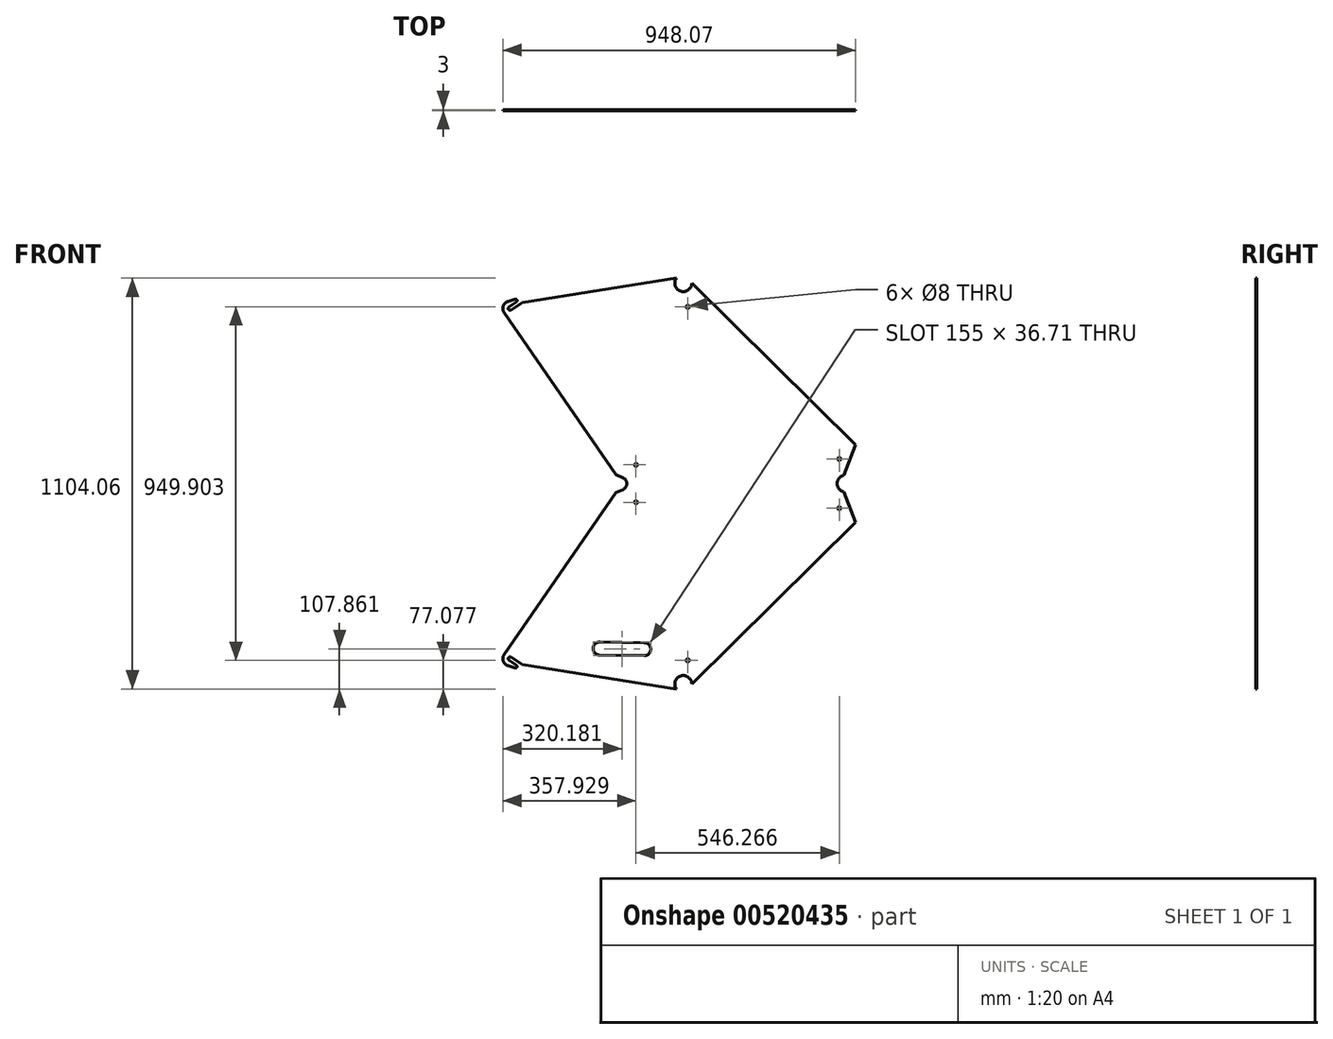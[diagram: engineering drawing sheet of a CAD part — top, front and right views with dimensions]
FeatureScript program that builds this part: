
annotation { "Feature Type Name" : "Feature", "Feature Type Description" : "" }
export const myFeature = defineFeature(function(context is Context, id is Id, definition is map)
    precondition{}
    {
        {
            var Q0;
            Q0=qCreatedBy(makeId("Front.planeOp"),FACE);
            var sketch = newSketch(context, id + "F0", { "sketchPlane" : qUnion([Q0])});
            skCircle(sketch, "E0", {"center": v(1053.9, -134.2) * mm, "radius": 17 * mm, "construction": true});
            skCircle(sketch, "E1", {"center": v(1053.9, -134.2) * mm, "radius": 21.5 * mm, "construction": true});
            skLineSegment(sketch, "E2", {"start": v(622.48, -20.32) * mm, "end": v(871.92, 345.36) * mm, "construction": true});
            skLineSegment(sketch, "E3", {"start": v(615.02, -14.4) * mm, "end": v(879.24, 372.95) * mm, "construction": true});
            skLineSegment(sketch, "E4", {"start": v(1053.9, -134.2) * mm, "end": v(865.03, 414.2) * mm, "construction": true});
            skLineSegment(sketch, "E5", {"start": v(1034.15, -125.7) * mm, "end": v(850, 409.01) * mm, "construction": true});
            skLineSegment(sketch, "E6", {"start": v(861.66, 381.3) * mm, "end": v(851.9, 409.67) * mm, "construction": true});
            skLineSegment(sketch, "E7", {"start": v(1064.21, -115.34) * mm, "end": v(880.07, 419.37) * mm, "construction": true});
            skLineSegment(sketch, "E8", {"start": v(1053.9, -134.2) * mm, "end": v(645.8, -73.78) * mm, "construction": true});
            skLineSegment(sketch, "E9", {"start": v(743.09, -99.4) * mm, "end": v(644.17, -84.76) * mm, "construction": true});
            skLineSegment(sketch, "E10", {"start": v(746.34, -77.44) * mm, "end": v(647.42, -62.8) * mm, "construction": true});
            skLineSegment(sketch, "E11", {"start": v(1035.36, -145.1) * mm, "end": v(841.66, -116.43) * mm, "construction": true});
            skLineSegment(sketch, "E12", {"start": v(1039.32, -118.4) * mm, "end": v(845.61, -89.72) * mm, "construction": true});
            skLineSegment(sketch, "E13", {"start": v(966.15, -134.86) * mm, "end": v(995.58, -139.21) * mm, "construction": true});
            skLineSegment(sketch, "E14", {"start": v(960.23, -139.03) * mm, "end": v(994.85, -144.16) * mm, "construction": true});
            skLineSegment(sketch, "E15", {"start": v(963.6, -143.58) * mm, "end": v(964.04, -140.6) * mm, "construction": true});
            skArc(sketch, "E16", {"start": v(959.64, -143) * mm, "mid": v(959.83, -143.73) * mm, "end": v(960.48, -144.13) * mm, "construction": true});
            skLineSegment(sketch, "E17", {"start": v(960.48, -144.13) * mm, "end": v(962.46, -144.42) * mm, "construction": true});
            skArc(sketch, "E18", {"start": v(962.46, -144.42) * mm, "mid": v(963.2, -144.23) * mm, "end": v(963.6, -143.58) * mm, "construction": true});
            skLineSegment(sketch, "E19", {"start": v(965.3, -133.72) * mm, "end": v(967.21, -120.86) * mm, "construction": true});
            skLineSegment(sketch, "E20", {"start": v(963, -120.24) * mm, "end": v(959.64, -143) * mm, "construction": true});
            skLineSegment(sketch, "E21", {"start": v(962.42, -124.2) * mm, "end": v(966.63, -124.82) * mm, "construction": true});
            skArc(sketch, "E22", {"start": v(965.17, -139.77) * mm, "mid": v(964.43, -139.95) * mm, "end": v(964.04, -140.6) * mm, "construction": true});
            skLineSegment(sketch, "E23", {"start": v(961.7, -129.14) * mm, "end": v(965.9, -129.76) * mm, "construction": true});
            skLineSegment(sketch, "E24", {"start": v(960.08, -126.38) * mm, "end": v(968.24, -127.58) * mm, "construction": true});
            skLineSegment(sketch, "E25", {"start": v(974.82, -141.2) * mm, "end": v(975.55, -136.25) * mm, "construction": true});
            skArc(sketch, "E26", {"start": v(965.3, -133.72) * mm, "mid": v(965.5, -134.46) * mm, "end": v(966.15, -134.86) * mm, "construction": true});
            skLineSegment(sketch, "E27", {"start": v(964.14, -119.4) * mm, "end": v(966.37, -119.73) * mm, "construction": true});
            skArc(sketch, "E28", {"start": v(964.14, -119.4) * mm, "mid": v(963.4, -119.58) * mm, "end": v(963, -120.24) * mm, "construction": true});
            skArc(sketch, "E29", {"start": v(967.21, -120.86) * mm, "mid": v(967.03, -120.12) * mm, "end": v(966.37, -119.73) * mm, "construction": true});
            skLineSegment(sketch, "E30", {"start": v(995.58, -139.21) * mm, "end": v(999.8, -144.9) * mm, "construction": true});
            skLineSegment(sketch, "E31", {"start": v(979.72, -143.94) * mm, "end": v(981.04, -135.04) * mm, "construction": true});
            skArc(sketch, "E32", {"start": v(995.7, -145.3) * mm, "mid": v(995.5, -144.55) * mm, "end": v(994.85, -144.16) * mm, "construction": true});
            skArc(sketch, "E33", {"start": v(995.25, -148.26) * mm, "mid": v(995.44, -149) * mm, "end": v(996.1, -149.4) * mm, "construction": true});
            skArc(sketch, "E34", {"start": v(998.07, -149.7) * mm, "mid": v(998.82, -149.5) * mm, "end": v(999.2, -148.85) * mm, "construction": true});
            skLineSegment(sketch, "E35", {"start": v(996.1, -149.4) * mm, "end": v(998.07, -149.7) * mm, "construction": true});
            skLineSegment(sketch, "E36", {"start": v(999.2, -148.85) * mm, "end": v(999.8, -144.9) * mm, "construction": true});
            skLineSegment(sketch, "E37", {"start": v(995.25, -148.26) * mm, "end": v(995.7, -145.3) * mm, "construction": true});
            skLineSegment(sketch, "E38", {"start": v(985.2, -142.73) * mm, "end": v(985.94, -137.79) * mm, "construction": true});
            skLineSegment(sketch, "E39", {"start": v(995.47, -146.78) * mm, "end": v(993.6, -159.38) * mm, "construction": true});
            skLineSegment(sketch, "E40", {"start": v(850, 409.01) * mm, "end": v(880.07, 419.37) * mm, "construction": true});
            skLineSegment(sketch, "E41", {"start": v(859.77, 380.65) * mm, "end": v(861.66, 381.3) * mm, "construction": true});
            skLineSegment(sketch, "E42", {"start": v(1053.92, -134.2) * mm, "end": v(1520.05, 326.73) * mm, "construction": true});
            skLineSegment(sketch, "E43", {"start": v(1076.92, -133.82) * mm, "end": v(1510.36, 294.78) * mm, "construction": true});
            skLineSegment(sketch, "E44", {"start": v(1060.7, -105.14) * mm, "end": v(1497.91, 327.2) * mm, "construction": true});
            skLineSegment(sketch, "E45", {"start": v(879.24, 372.95) * mm, "end": v(1402.67, 372.95) * mm, "construction": true});
            skLineSegment(sketch, "E46", {"start": v(901.53, 357.05) * mm, "end": v(1486.45, 357.05) * mm, "construction": true});
            skLineSegment(sketch, "E47", {"start": v(890.58, 388.85) * mm, "end": v(1474.25, 388.85) * mm, "construction": true});
            skArc(sketch, "E48", {"start": v(1486.5, 356.93) * mm, "mid": v(1487.54, 375.64) * mm, "end": v(1474.25, 388.85) * mm, "construction": true});
            skArc(sketch, "E49", {"start": v(890.58, 388.85) * mm, "mid": v(888.92, 370.5) * mm, "end": v(901.53, 357.05) * mm, "construction": true});
            skArc(sketch, "E50", {"start": v(1510.36, 294.78) * mm, "mid": v(1511.76, 313.92) * mm, "end": v(1497.91, 327.2) * mm, "construction": true});
            skArc(sketch, "E51", {"start": v(919.09, -223.5) * mm, "mid": v(918.34, -223.31) * mm, "end": v(917.6, -223.13) * mm, "construction": true});
            skFitSpline(sketch, "E52", {"points": [v(871.92, 345.36) * mm, v(875.7, 355.52) * mm, v(881.2, 370.3) * mm, v(868.26, 368.37) * mm, v(864.2, 367.77) * mm], "construction": true});
            skArc(sketch, "E53", {"start": v(591.11, -61.72) * mm, "mid": v(584.1, -63.16) * mm, "end": v(585.54, -70.17) * mm});
            skLineSegment(sketch, "E54", {"start": v(585.54, -70.17) * mm, "end": v(605.08, -83.05) * mm});
            skLineSegment(sketch, "E55", {"start": v(601.2, -91.02) * mm, "end": v(582.02, -84.5) * mm});
            skLineSegment(sketch, "E56", {"start": v(584.15, -63.19) * mm, "end": v(613.37, -82.46) * mm, "construction": true});
            skLineSegment(sketch, "E57", {"start": v(607.46, -8.63) * mm, "end": v(607.4, -8.7) * mm, "construction": true});
            skLineSegment(sketch, "E58", {"start": v(644.18, -84.66) * mm, "end": v(644.29, -83.94) * mm, "construction": true});
            skLineSegment(sketch, "E59", {"start": v(591.11, -61.72) * mm, "end": v(620.67, -81.2) * mm});
            skLineSegment(sketch, "E60", {"start": v(644.18, -84.66) * mm, "end": v(622.66, -81.47) * mm, "construction": true});
            skArc(sketch, "E61", {"start": v(644.63, -83.68) * mm, "mid": v(644.4, -83.74) * mm, "end": v(644.29, -83.94) * mm, "construction": true});
            skLineSegment(sketch, "E62", {"start": v(644.18, -84.66) * mm, "end": v(644.19, -84.63) * mm, "construction": true});
            skArc(sketch, "E63", {"start": v(601.2, -91.02) * mm, "mid": v(606.49, -88.67) * mm, "end": v(605.08, -83.05) * mm});
            skArc(sketch, "E64", {"start": v(617.78, -52.64) * mm, "mid": v(628.06, -58.54) * mm, "end": v(639.47, -61.73) * mm, "construction": true});
            skLineSegment(sketch, "E65", {"start": v(670.48, -77.43) * mm, "end": v(577.33, -63.64) * mm, "construction": true});
            skLineSegment(sketch, "E66", {"start": v(647.4, -62.9) * mm, "end": v(639.47, -61.73) * mm, "construction": true});
            skArc(sketch, "E67", {"start": v(647.3, -63.56) * mm, "mid": v(647.36, -63.78) * mm, "end": v(647.56, -63.9) * mm, "construction": true});
            skLineSegment(sketch, "E68", {"start": v(647.3, -63.56) * mm, "end": v(647.4, -62.9) * mm, "construction": true});
            skArc(sketch, "E69", {"start": v(614, -32.51) * mm, "mid": v(611.92, -43.32) * mm, "end": v(617.78, -52.64) * mm, "construction": true});
            skLineSegment(sketch, "E70", {"start": v(614, -32.51) * mm, "end": v(622.56, -20.17) * mm, "construction": true});
            skLineSegment(sketch, "E71", {"start": v(577.33, -63.64) * mm, "end": v(629.71, 4.8) * mm, "construction": true});
            skArc(sketch, "E72", {"start": v(572.75, -54.03) * mm, "mid": v(569.56, -71.65) * mm, "end": v(582.02, -84.5) * mm});
            skLineSegment(sketch, "E73", {"start": v(607.46, -8.63) * mm, "end": v(608.42, -9.36) * mm, "construction": true});
            skArc(sketch, "E74", {"start": v(621.55, -19.02) * mm, "mid": v(621.5, -19.24) * mm, "end": v(621.6, -19.44) * mm, "construction": true});
            skLineSegment(sketch, "E75", {"start": v(621.6, -19.44) * mm, "end": v(622.56, -20.17) * mm, "construction": true});
            skArc(sketch, "E76", {"start": v(608.42, -9.36) * mm, "mid": v(608.64, -9.42) * mm, "end": v(608.84, -9.3) * mm, "construction": true});
            skLineSegment(sketch, "E77", {"start": v(608.42, -9.36) * mm, "end": v(607.46, -8.63) * mm, "construction": true});
            skLineSegment(sketch, "E78", {"start": v(619.71, -24.29) * mm, "end": v(604.42, -12.6) * mm, "construction": true});
            skCircle(sketch, "E79", {"center": v(600.85, -74.2) * mm, "radius": 5 * mm, "construction": true});
            skLineSegment(sketch, "E80", {"start": v(621.6, -19.44) * mm, "end": v(608.42, -9.36) * mm, "construction": true});
            skLineSegment(sketch, "E81", {"start": v(841.66, -116.43) * mm, "end": v(743.09, -99.4) * mm, "construction": true});
            skLineSegment(sketch, "E82", {"start": v(746.34, -77.44) * mm, "end": v(845.61, -89.72) * mm, "construction": true});
            skEllipse(sketch, "E83", {"center": v(843.64, -103.07) * mm, "majorRadius": 13.5 * mm, "minorRadius": 8.5 * mm, "majorAxis": v(-0.15, -0.99), "construction": true});
            skCircle(sketch, "E84", {"center": v(795.03, 249.5) * mm, "radius": 9.5 * mm, "construction": true});
            skLineSegment(sketch, "E85", {"start": v(796.02, 244.3) * mm, "end": v(795.95, 244.64) * mm, "construction": true});
            skLineSegment(sketch, "E86", {"start": v(796.02, 244.3) * mm, "end": v(789.82, 248.52) * mm, "construction": true});
            skLineSegment(sketch, "E87", {"start": v(784, 242.2) * mm, "end": v(792.26, 236.56) * mm, "construction": true});
            skLineSegment(sketch, "E88", {"start": v(792.26, 236.56) * mm, "end": v(793.8, 238.84) * mm, "construction": true});
            skLineSegment(sketch, "E89", {"start": v(791.91, 236.5) * mm, "end": v(792.26, 236.56) * mm, "construction": true});
            skLineSegment(sketch, "E90", {"start": v(795.95, 244.64) * mm, "end": v(790.17, 248.58) * mm, "construction": true});
            skLineSegment(sketch, "E91", {"start": v(791.91, 236.5) * mm, "end": v(784.06, 241.85) * mm, "construction": true});
            skLineSegment(sketch, "E92", {"start": v(789.96, 238.43) * mm, "end": v(794.75, 245.46) * mm, "construction": true});
            skLineSegment(sketch, "E93", {"start": v(790.2, 238) * mm, "end": v(795.12, 245.2) * mm, "construction": true});
            skLineSegment(sketch, "E94", {"start": v(793.8, 238.84) * mm, "end": v(785.55, 244.47) * mm, "construction": true});
            skLineSegment(sketch, "E95", {"start": v(792.78, 239.54) * mm, "end": v(796.02, 244.3) * mm, "construction": true});
            skArc(sketch, "E96", {"start": v(962.06, -126.67) * mm, "mid": v(930.44, 82.62) * mm, "end": v(787.99, 239.18) * mm, "construction": true});
            skLineSegment(sketch, "E97", {"start": v(702.12, -93.34) * mm, "end": v(670.46, -88.65) * mm, "construction": true});
            skCircle(sketch, "E98", {"center": v(1054.53, -129.2) * mm, "radius": 89.9 * mm, "construction": true});
            skCircle(sketch, "E99", {"center": v(600.85, -74.2) * mm, "radius": 41.4 * mm, "construction": true});
            skLineSegment(sketch, "E100", {"start": v(1055.81, -39.3) * mm, "end": v(601.44, -32.8) * mm, "construction": true});
            skLineSegment(sketch, "E101", {"start": v(1469.36, 401.56) * mm, "end": v(1507.64, 416.26) * mm, "construction": true});
            skLineSegment(sketch, "E102", {"start": v(1507.64, 416.26) * mm, "end": v(1552.44, 299.56) * mm, "construction": true});
            skLineSegment(sketch, "E103", {"start": v(1552.44, 299.56) * mm, "end": v(1514.16, 284.87) * mm, "construction": true});
            skLineSegment(sketch, "E104", {"start": v(1514.16, 284.87) * mm, "end": v(1469.36, 401.56) * mm, "construction": true});
            skLineSegment(sketch, "E105", {"start": v(1516.78, 301.13) * mm, "end": v(1076.92, -133.82) * mm});
            skLineSegment(sketch, "E106", {"start": v(572.75, -54.03) * mm, "end": v(878.77, 388.85) * mm});
            skArc(sketch, "E107", {"start": v(1076.92, -133.82) * mm, "mid": v(1046.89, -112.3) * mm, "end": v(1035, -147.28) * mm});
            skLineSegment(sketch, "E108.trimOffspring", {"start": v(1035, -147.28) * mm, "end": v(620.67, -81.2) * mm});
            skCircle(sketch, "E109", {"center": v(926.64, 354.5) * mm, "radius": 4 * mm});
            skCircle(sketch, "E110", {"center": v(1472.9, 338.57) * mm, "radius": 4 * mm});
            skCircle(sketch, "E111", {"center": v(1065.92, -70.2) * mm, "radius": 4 * mm});
            skLineSegment(sketch, "E112", {"start": v(1053.92, -134.2) * mm, "end": v(1237.3, -134.2) * mm, "construction": true});
            skLineSegment(sketch, "E113", {"start": v(1053.92, -134.2) * mm, "end": v(1053.92, 23.57) * mm, "construction": true});
            skCircle(sketch, "E114", {"center": v(866.64, 414.5) * mm, "radius": 25 * mm, "construction": true});
            skCircle(sketch, "E115", {"center": v(1489.1, 401.54) * mm, "radius": 28.6 * mm, "construction": true});
            skLineSegment(sketch, "E116", {"start": v(1516.78, 301.13) * mm, "end": v(1482.36, 388.85) * mm});
            skLineSegment(sketch, "E117.trimOffspring", {"start": v(878.77, 388.85) * mm, "end": v(1482.36, 388.85) * mm});
            skSolve(sketch);
        }
        {
            var Q0;
            Q0 = qSketchRegion(id + "F0", true);
            extrude(context, id + "F1", {"entities" : qUnion([Q0]), "depth" : 3 * mm, "offsetDistance" : 25 * mm});
        }
        {
            var Q0;
            Q0=makeQuery(id+"F1.opExtrude","SWEPT_FACE",FACE,{"disambiguationData":[OSD([sQuery(id+"F0.wireOp",EDGE,"E117.trimOffspring")])]});
            cPlane(context, id + "F2", {"entities" : qUnion([Q0]), "cplaneType" : CPlaneType.OFFSET, "offset" : 15.9 * mm, "width" : 150 * mm, "height" : 150 * mm});
        }
        {
            var Q0;
            Q0=makeQuery(id+"F1.opExtrude","SWEPT_BODY",BODY,{"disambiguationData":[OSD([sQuery(id+"F0.wireOp",EDGE,"E53"),sQuery(id+"F0.wireOp",EDGE,"E54"),sQuery(id+"F0.wireOp",EDGE,"E55"),sQuery(id+"F0.wireOp",EDGE,"E59"),sQuery(id+"F0.wireOp",EDGE,"c0fece56-cd10-4327-9040-2cab23e675d4"),sQuery(id+"F0.wireOp",EDGE,"E63"),sQuery(id+"F0.wireOp",EDGE,"E72"),sQuery(id+"F0.wireOp",EDGE,"PVY0APLz-6rdr-JrDk-CvCb-vWmYWycaJObT"),sQuery(id+"F0.wireOp",EDGE,"rSiPkJzu-22ck-wLmw-T34Z-YrS7vC3DeLN9"),sQuery(id+"F0.wireOp",EDGE,"E105"),sQuery(id+"F0.wireOp",EDGE,"E106"),sQuery(id+"F0.wireOp",EDGE,"E107"),sQuery(id+"F0.wireOp",EDGE,"E108.trimOffspring")])]});
            var Q1;
            Q1=qCreatedBy(id+"F2.planeOp",FACE);
            mirror(context, id + "F3", {"entities" : qUnion([Q0]), "mirrorPlane" : qUnion([Q1])});
        }
        {
            var Q0;
            Q0=makeQuery(id+"F1.opExtrude","CAP_FACE",FACE,{"disambiguationData":[OSD([sQuery(id+"F0.wireOp",EDGE,"E53"),sQuery(id+"F0.wireOp",EDGE,"E54"),sQuery(id+"F0.wireOp",EDGE,"E55"),sQuery(id+"F0.wireOp",EDGE,"E59"),sQuery(id+"F0.wireOp",EDGE,"c0fece56-cd10-4327-9040-2cab23e675d4"),sQuery(id+"F0.wireOp",EDGE,"E63"),sQuery(id+"F0.wireOp",EDGE,"E72"),sQuery(id+"F0.wireOp",EDGE,"PVY0APLz-6rdr-JrDk-CvCb-vWmYWycaJObT"),sQuery(id+"F0.wireOp",EDGE,"rSiPkJzu-22ck-wLmw-T34Z-YrS7vC3DeLN9"),sQuery(id+"F0.wireOp",EDGE,"E105"),sQuery(id+"F0.wireOp",EDGE,"E106"),sQuery(id+"F0.wireOp",EDGE,"E107"),sQuery(id+"F0.wireOp",EDGE,"E108.trimOffspring")])],"isStart":false});
            var sketch = newSketch(context, id + "F4", { "sketchPlane" : qUnion([Q0])});
            skArc(sketch, "E118", {"start": v(1484.73, 426.68) * mm, "mid": v(1467.24, 404.75) * mm, "end": v(1484.73, 382.81) * mm});
            skArc(sketch, "E119", {"start": v(891.59, 388.85) * mm, "mid": v(901.78, 404.75) * mm, "end": v(891.59, 420.65) * mm});
            skLineSegment(sketch, "E120", {"start": v(884.28, 404.75) * mm, "end": v(1489.74, 404.75) * mm, "construction": true});
            skLineSegment(sketch, "E121", {"start": v(891.59, 420.65) * mm, "end": v(872.8, 429.29) * mm});
            skLineSegment(sketch, "E122", {"start": v(891.59, 388.85) * mm, "end": v(872.8, 380.21) * mm});
            skLineSegment(sketch, "E123.0", {"start": v(1516.78, 508.37) * mm, "end": v(1482.36, 420.65) * mm, "construction": true});
            skLineSegment(sketch, "E124", {"start": v(1482.36, 388.85) * mm, "end": v(1516.78, 301.13) * mm, "construction": true});
            skLineSegment(sketch, "E125", {"start": v(891.59, 420.65) * mm, "end": v(1473.82, 420.65) * mm});
            skLineSegment(sketch, "E126", {"start": v(891.59, 388.85) * mm, "end": v(1473.82, 388.85) * mm});
            skSolve(sketch);
        }
        {
            var Q0;
            Q0 = qSketchRegion(id + "F4", true);
            var Q1;
            Q1=makeQuery(id+"F3.opPattern","COPY",FACE,{"derivedFrom":makeQuery(id+"F1.opExtrude","CAP_FACE",FACE,{"disambiguationData":[OSD([sQuery(id+"F0.wireOp",EDGE,"E53"),sQuery(id+"F0.wireOp",EDGE,"E54"),sQuery(id+"F0.wireOp",EDGE,"E55"),sQuery(id+"F0.wireOp",EDGE,"E59"),sQuery(id+"F0.wireOp",EDGE,"c0fece56-cd10-4327-9040-2cab23e675d4"),sQuery(id+"F0.wireOp",EDGE,"E63"),sQuery(id+"F0.wireOp",EDGE,"E72"),sQuery(id+"F0.wireOp",EDGE,"PVY0APLz-6rdr-JrDk-CvCb-vWmYWycaJObT"),sQuery(id+"F0.wireOp",EDGE,"rSiPkJzu-22ck-wLmw-T34Z-YrS7vC3DeLN9"),sQuery(id+"F0.wireOp",EDGE,"E105"),sQuery(id+"F0.wireOp",EDGE,"E106"),sQuery(id+"F0.wireOp",EDGE,"E107"),sQuery(id+"F0.wireOp",EDGE,"E108.trimOffspring")])],"isStart":true}),"instanceName":"1"});
            extrude(context, id + "F5", {"entities" : qUnion([Q0]), "operationType" : NewBodyOperationType.ADD, "endBound" : BoundingType.UP_TO_SURFACE, "oppositeDirection" : true, "depth" : 65 * mm, "endBoundEntityFace" : qUnion([Q1]), "offsetDistance" : 25 * mm});
        }
        {
            var Q0;
            {var subQ0=makeQuery(id+"F1.opExtrude","CAP_FACE",FACE,{"disambiguationData":[OSD([sQuery(id+"F0.wireOp",EDGE,"E53"),sQuery(id+"F0.wireOp",EDGE,"E54"),sQuery(id+"F0.wireOp",EDGE,"E55"),sQuery(id+"F0.wireOp",EDGE,"E59"),sQuery(id+"F0.wireOp",EDGE,"E63"),sQuery(id+"F0.wireOp",EDGE,"E72"),sQuery(id+"F0.wireOp",EDGE,"E105"),sQuery(id+"F0.wireOp",EDGE,"E106"),sQuery(id+"F0.wireOp",EDGE,"E107"),sQuery(id+"F0.wireOp",EDGE,"E108.trimOffspring"),sQuery(id+"F0.wireOp",EDGE,"E109"),sQuery(id+"F0.wireOp",EDGE,"E110"),sQuery(id+"F0.wireOp",EDGE,"E111"),sQuery(id+"F0.wireOp",EDGE,"E116"),sQuery(id+"F0.wireOp",EDGE,"E117.trimOffspring")])],"isStart":false});Q0=makeQuery(id+"F5.boolean.opBoolean","MERGE",FACE,{"derivedFrom":[subQ0,makeQuery(id+"F3.opPattern","COPY",FACE,{"derivedFrom":subQ0,"instanceName":"1"}),makeQuery(id+"F5.opExtrude","CAP_FACE",FACE,{"disambiguationData":[OSD([sQuery(id+"F4.wireOp",EDGE,"E118"),sQuery(id+"F4.wireOp",EDGE,"E119"),sQuery(id+"F4.wireOp",EDGE,"E125"),sQuery(id+"F4.wireOp",EDGE,"E126")])],"isStart":true})]});}
            var sketch = newSketch(context, id + "F6", { "sketchPlane" : qUnion([Q0])});
            skLineSegment(sketch, "E127.0", {"start": v(891.59, 420.65) * mm, "end": v(872.8, 429.29) * mm});
            skLineSegment(sketch, "E127.1", {"start": v(891.59, 388.85) * mm, "end": v(872.8, 380.21) * mm});
            skArc(sketch, "E128.0", {"start": v(891.59, 388.85) * mm, "mid": v(901.78, 404.75) * mm, "end": v(891.59, 420.65) * mm});
            skLineSegment(sketch, "E129", {"start": v(872.8, 429.29) * mm, "end": v(872.8, 380.21) * mm});
            skArc(sketch, "E130.0", {"start": v(1484.73, 426.68) * mm, "mid": v(1467.24, 404.75) * mm, "end": v(1484.73, 382.81) * mm});
            skLineSegment(sketch, "E131", {"start": v(1484.73, 426.68) * mm, "end": v(1484.73, 382.81) * mm});
            skSolve(sketch);
        }
        {
            var Q0;
            {var subQ0=makeQuery(id+"F1.opExtrude","CAP_FACE",FACE,{"disambiguationData":[OSD([sQuery(id+"F0.wireOp",EDGE,"E53"),sQuery(id+"F0.wireOp",EDGE,"E54"),sQuery(id+"F0.wireOp",EDGE,"E55"),sQuery(id+"F0.wireOp",EDGE,"E59"),sQuery(id+"F0.wireOp",EDGE,"E63"),sQuery(id+"F0.wireOp",EDGE,"E72"),sQuery(id+"F0.wireOp",EDGE,"PVY0APLz-6rdr-JrDk-CvCb-vWmYWycaJObT"),sQuery(id+"F0.wireOp",EDGE,"rSiPkJzu-22ck-wLmw-T34Z-YrS7vC3DeLN9"),sQuery(id+"F0.wireOp",EDGE,"E105"),sQuery(id+"F0.wireOp",EDGE,"E106"),sQuery(id+"F0.wireOp",EDGE,"E107"),sQuery(id+"F0.wireOp",EDGE,"E108.trimOffspring"),sQuery(id+"F0.wireOp",EDGE,"E109"),sQuery(id+"F0.wireOp",EDGE,"E110"),sQuery(id+"F0.wireOp",EDGE,"E111")])],"isStart":false});Q0=makeQuery(id+"F5.boolean.opBoolean","MERGE",FACE,{"derivedFrom":[subQ0,makeQuery(id+"F3.opPattern","COPY",FACE,{"derivedFrom":subQ0,"instanceName":"1"}),makeQuery(id+"F5.opExtrude","CAP_FACE",FACE,{"disambiguationData":[OSD([sQuery(id+"F4.wireOp",EDGE,"yLFeXnhX-FHJ1-lWFD-LUYU-IVhkZNTNpous"),sQuery(id+"F4.wireOp",EDGE,"25Roz2r3-I6Ic-58va-7k2N-V37a2FIcnueW"),sQuery(id+"F4.wireOp",EDGE,"Mdtmx1y3-Aq5y-VBCD-G2xE-9g1DUSUnupkp"),sQuery(id+"F4.wireOp",EDGE,"31XSQ7MP-bYWI-LpWw-hrBR-gacfVsKKRKhD")])],"isStart":true})]});}
            var sketch = newSketch(context, id + "F7", { "sketchPlane" : qUnion([Q0])});
            skLineSegment(sketch, "E132.bottom", {"start": v(829.14, -21.06) * mm, "end": v(949.14, -22.78) * mm});
            skLineSegment(sketch, "E132.top", {"start": v(828.64, -56.06) * mm, "end": v(948.64, -57.78) * mm});
            skArc(sketch, "E133", {"start": v(829.14, -21.06) * mm, "mid": v(811.4, -38.3) * mm, "end": v(828.64, -56.06) * mm});
            skArc(sketch, "E134", {"start": v(948.64, -57.78) * mm, "mid": v(966.39, -40.53) * mm, "end": v(949.14, -22.78) * mm});
            skSolve(sketch);
        }
        {
            var Q0;
            Q0 = qSketchRegion(id + "F7", true);
            extrude(context, id + "F8", {"entities" : qUnion([Q0]), "operationType" : NewBodyOperationType.REMOVE, "oppositeDirection" : true, "depth" : 25 * mm, "offsetDistance" : 25 * mm});
        }
        {
            var Q0;
            Q0 = qSketchRegion(id + "F6", true);
            extrude(context, id + "F9", {"entities" : qUnion([Q0]), "operationType" : NewBodyOperationType.REMOVE, "oppositeDirection" : true, "depth" : 25 * mm, "offsetDistance" : 25 * mm});
        }
    });
